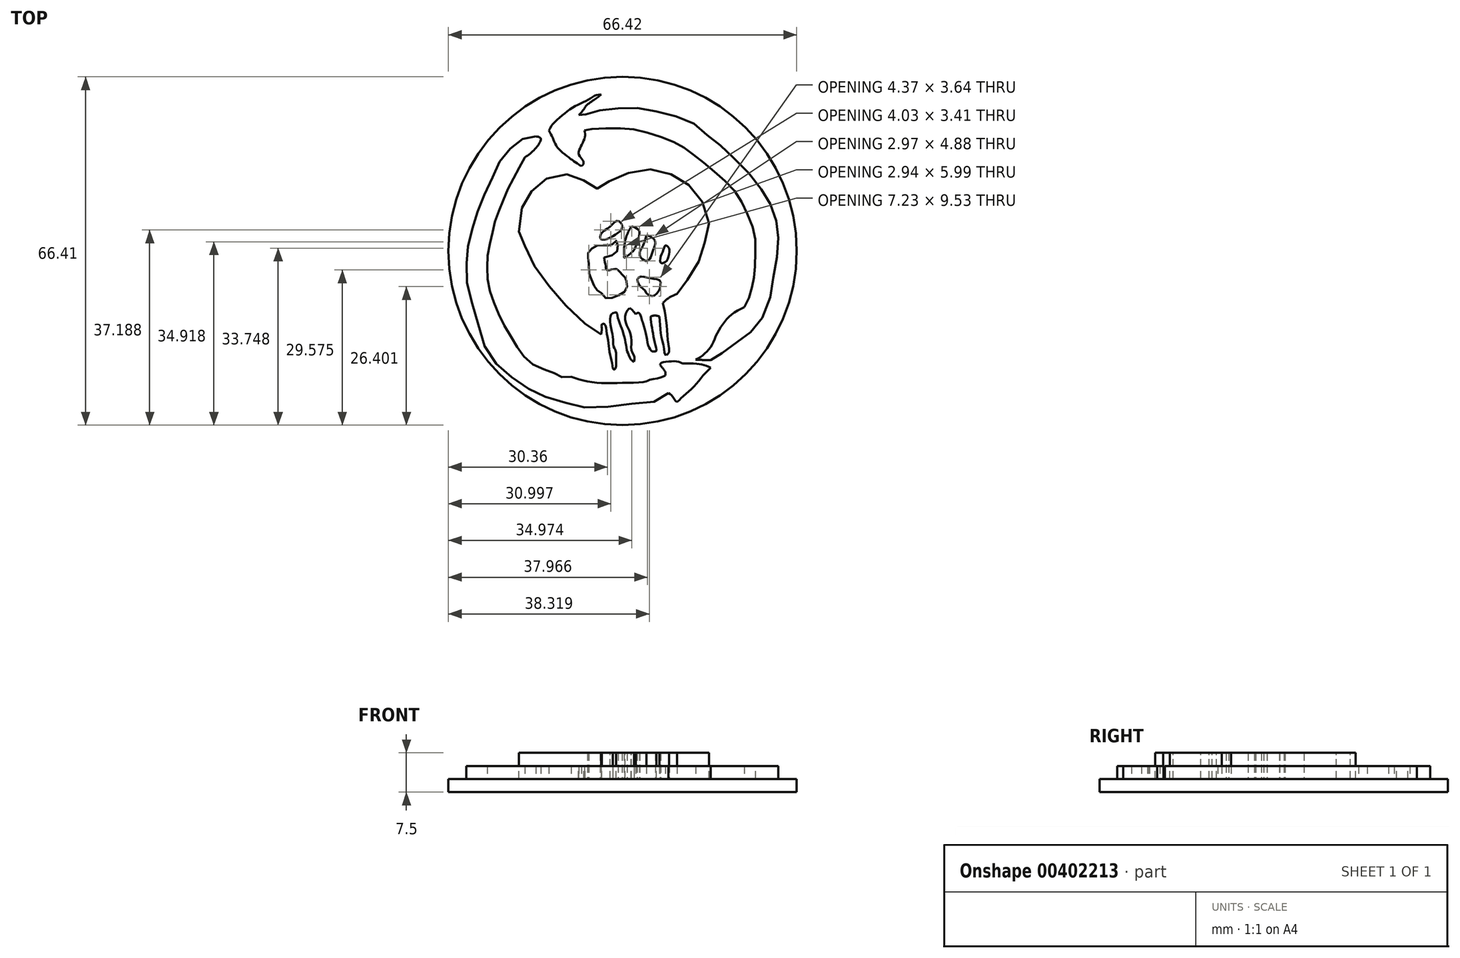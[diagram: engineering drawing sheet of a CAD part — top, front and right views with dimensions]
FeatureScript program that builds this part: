
annotation { "Feature Type Name" : "Feature", "Feature Type Description" : "" }
export const myFeature = defineFeature(function(context is Context, id is Id, definition is map)
    precondition{}
    {
        {
            var Q0;
            Q0=qCreatedBy(makeId("Top.planeOp"),FACE);
            var sketch = newSketch(context, id + "F0", { "sketchPlane" : qUnion([Q0])});
            skLineSegment(sketch, "E0", {"start": v(23.35, 42.94) * mm, "end": v(23.35, 78.4) * mm, "construction": true});
            skLineSegment(sketch, "E1", {"start": v(83.35, 42.94) * mm, "end": v(83.35, 78.4) * mm, "construction": true});
            skFitSpline(sketch, "E2", {"points": [v(67.3, 27.12) * mm, v(68.35, 27.69) * mm, v(69.45, 28.7) * mm, v(70.34, 29.8) * mm, v(70.99, 31.25) * mm, v(71.88, 33) * mm, v(73, 34.57) * mm, v(74.43, 35.94) * mm, v(76.6, 37.12) * mm], "startDerivative": vector(10.15, 4.67) * mm, "endDerivative": vector(15.46, 7.4) * mm});
            skFitSpline(sketch, "E3", {"points": [v(76.6, 37.12) * mm, v(77.58, 39.29) * mm, v(78.26, 41.84) * mm, v(78.56, 43.89) * mm, v(78.7, 48.13) * mm, v(78.44, 51.6) * mm, v(76.83, 55.52) * mm, v(75.11, 58.81) * mm, v(72.15, 61.84) * mm, v(68.8, 64.72) * mm, v(66, 66.88) * mm, v(63.48, 68.43) * mm, v(59.62, 69.94) * mm, v(55.35, 71.04) * mm, v(51.17, 71.25) * mm, v(47.04, 71.04) * mm, v(46.1, 70.83) * mm], "startDerivative": vector(19.98, 39.48) * mm, "endDerivative": vector(-22.77, -6.63) * mm});
            skFitSpline(sketch, "E4", {"points": [v(46.1, 70.83) * mm, v(46.23, 70.04) * mm, v(46.1, 69.31) * mm, v(45.66, 68.29) * mm, v(45.2, 67.32) * mm, v(44.97, 66.68) * mm, v(45.17, 65.94) * mm, v(45.63, 65.3) * mm, v(45.89, 64.83) * mm, v(45.89, 64.4) * mm, v(45.5, 64.03) * mm], "startDerivative": vector(1.88, -7.74) * mm, "endDerivative": vector(-5.78, -3.74) * mm});
            skFitSpline(sketch, "E5", {"points": [v(45.5, 64.03) * mm, v(44.46, 64.68) * mm, v(42.97, 65.75) * mm, v(40.94, 67.6) * mm, v(40.14, 69.15) * mm, v(39.32, 70.83) * mm], "startDerivative": vector(-6.2, 3.8) * mm, "endDerivative": vector(-4.35, 8.46) * mm});
            skFitSpline(sketch, "E6", {"points": [v(39.32, 70.83) * mm, v(40.06, 72.03) * mm, v(41.7, 73.56) * mm, v(43.58, 75.03) * mm, v(45.5, 76.06) * mm, v(46.98, 76.77) * mm, v(48.1, 77.5) * mm, v(49.24, 77.67) * mm], "startDerivative": vector(4.72, 9.25) * mm, "endDerivative": vector(9.94, 0.27) * mm});
            skFitSpline(sketch, "E7", {"points": [v(49.24, 77.67) * mm, v(48.43, 77) * mm, v(47.34, 76.29) * mm, v(46.35, 75.43) * mm, v(45.7, 74.52) * mm, v(45, 73.77) * mm], "startDerivative": vector(-3.85, -3.64) * mm, "endDerivative": vector(-3.85, -3.82) * mm});
            skFitSpline(sketch, "E8", {"points": [v(45, 73.77) * mm, v(45, 73.45) * mm, v(45.5, 73.58) * mm, v(47.34, 74.19) * mm, v(49.24, 74.71) * mm, v(52.43, 75.03) * mm, v(55.9, 75.11) * mm, v(59.24, 74.57) * mm, v(63.09, 73.62) * mm, v(66.58, 72.4) * mm, v(68.82, 70.55) * mm, v(70.71, 68.97) * mm, v(73.1, 67.07) * mm, v(75.28, 64.81) * mm, v(78.67, 61.33) * mm, v(80.4, 58.67) * mm, v(81.8, 56.27) * mm, v(82.74, 53.22) * mm, v(83.03, 50.62) * mm, v(82.85, 47.24) * mm, v(82.18, 43.21) * mm, v(81.65, 39.65) * mm, v(80.13, 35.33) * mm, v(78.05, 32.63) * mm, v(76.06, 31.08) * mm, v(73.43, 29.15) * mm, v(71.3, 27.7) * mm, v(70.18, 27.03) * mm], "startDerivative": vector(-5.92, -32.65) * mm, "endDerivative": vector(-40.98, -23.98) * mm});
            skFitSpline(sketch, "E9", {"points": [v(70.18, 27.03) * mm, v(69.09, 27.03) * mm, v(67.3, 27.12) * mm], "startDerivative": vector(-2.34, -0.03) * mm, "endDerivative": vector(-3.37, 0.2) * mm});
            skFitSpline(sketch, "E10", {"points": [v(36.82, 69.7) * mm, v(35.14, 69.55) * mm, v(33.17, 68.46) * mm, v(31.5, 66.83) * mm, v(29.77, 64.64) * mm, v(28.66, 62.13) * mm, v(27.1, 58.81) * mm, v(25.87, 55.87) * mm, v(24.97, 52.87) * mm, v(24.15, 50.12) * mm, v(23.69, 46.72) * mm, v(23.58, 44.48) * mm, v(23.94, 39.9) * mm, v(25.36, 35.88) * mm, v(26.4, 31.22) * mm, v(28.6, 27.12) * mm, v(31.3, 24.44) * mm, v(34.8, 22) * mm, v(37.4, 20.45) * mm, v(41.56, 19.18) * mm, v(45, 18.16) * mm, v(50.1, 18.1) * mm, v(55.46, 18.76) * mm, v(59.94, 19.22) * mm, v(62.1, 20.72) * mm], "startDerivative": vector(-57, 0.93) * mm, "endDerivative": vector(51.79, 49.17) * mm});
            skFitSpline(sketch, "E11", {"points": [v(62.1, 20.72) * mm, v(62.73, 20.28) * mm, v(63.44, 19.27) * mm, v(63.77, 19.11) * mm, v(64.78, 20.03) * mm, v(67, 22) * mm, v(68.9, 24.3) * mm, v(69.98, 25.36) * mm, v(70.18, 25.59) * mm], "startDerivative": vector(6.6, -3.28) * mm, "endDerivative": vector(2.54, 3.24) * mm});
            skFitSpline(sketch, "E12", {"points": [v(70.18, 25.59) * mm, v(68.84, 26.08) * mm, v(67.04, 26.36) * mm, v(64.95, 26.4) * mm, v(64.58, 26.49) * mm, v(63.8, 26.77) * mm, v(62.1, 26.75) * mm, v(60.72, 26.5) * mm, v(60.5, 26.1) * mm], "startDerivative": vector(-9.56, 3.9) * mm, "endDerivative": vector(-1.36, -5.85) * mm});
            skFitSpline(sketch, "E13", {"points": [v(60.5, 26.1) * mm, v(60.93, 25.59) * mm, v(61.5, 24.72) * mm, v(61.51, 24.12) * mm], "startDerivative": vector(1.24, -1.48) * mm, "endDerivative": vector(-0.27, -1.93) * mm});
            skFitSpline(sketch, "E14", {"points": [v(61.51, 24.12) * mm, v(60.54, 23.66) * mm, v(58.35, 23.24) * mm, v(57.8, 22.92) * mm, v(54.5, 22.71) * mm, v(49.9, 22.64) * mm, v(46.35, 23.01) * mm, v(43.58, 23.88) * mm], "startDerivative": vector(-8.1, -5.35) * mm, "endDerivative": vector(-17.12, 6.22) * mm});
            skFitSpline(sketch, "E15", {"points": [v(43.58, 23.88) * mm, v(41.49, 23.88) * mm, v(39.92, 24.74) * mm, v(36.88, 25.85) * mm, v(34.29, 28.06) * mm, v(32.52, 30.77) * mm, v(30.51, 34.2) * mm, v(29.01, 37.53) * mm, v(27.88, 40.85) * mm, v(27.55, 44.26) * mm, v(27.7, 47.57) * mm, v(28.47, 50.94) * mm, v(29.1, 53.73) * mm, v(30.23, 56.55) * mm, v(31.54, 59.7) * mm, v(33.14, 62.78) * mm, v(34.71, 65.67) * mm], "startDerivative": vector(-44.4, -5.35) * mm, "endDerivative": vector(24.37, 45.13) * mm});
            skFitSpline(sketch, "E16", {"points": [v(34.71, 65.67) * mm, v(36.23, 66.86) * mm, v(37.41, 68.25) * mm, v(37.76, 69.12) * mm, v(37.55, 69.47) * mm, v(36.82, 69.7) * mm], "startDerivative": vector(5.88, 4.17) * mm, "endDerivative": vector(-4.96, 1.04) * mm});
            skFitSpline(sketch, "E17", {"points": [v(49.24, 31.89) * mm, v(46.77, 33.5) * mm, v(42.83, 37.12) * mm, v(39.32, 41.14) * mm, v(36.4, 45.23) * mm, v(34.71, 48.82) * mm, v(33.8, 49.97) * mm, v(33.8, 54.46) * mm, v(34.71, 57.4) * mm, v(36.82, 60.1) * mm, v(39.32, 61.85) * mm, v(42.88, 62.45) * mm, v(45, 61.85) * mm, v(47.87, 59.9) * mm, v(48.52, 59.75) * mm, v(49.24, 60.2) * mm, v(51.66, 61.55) * mm, v(55.16, 62.9) * mm, v(59.15, 63.4) * mm, v(62.7, 62.4) * mm, v(65.74, 60.65) * mm, v(68.18, 57.86) * mm, v(69.78, 53.81) * mm, v(69.42, 50.7) * mm, v(68.3, 47.32) * mm, v(67.3, 44.53) * mm, v(64.91, 41.33) * mm, v(63.73, 39.67) * mm], "startDerivative": vector(-63.83, 44.64) * mm, "endDerivative": vector(-34.2, -51.43) * mm});
            skFitSpline(sketch, "E18", {"points": [v(63.73, 39.67) * mm, v(62.1, 38.84) * mm, v(61.03, 37.92) * mm], "startDerivative": vector(-3.27, -1.45) * mm, "endDerivative": vector(-2.1, -2.05) * mm});
            skFitSpline(sketch, "E19", {"points": [v(61.03, 37.92) * mm, v(61.51, 35.7) * mm, v(61.83, 32.7) * mm, v(62.1, 30.03) * mm, v(62.1, 28.26) * mm, v(61.51, 28.03) * mm, v(61.25, 29.15) * mm, v(60.84, 31.1) * mm, v(60.54, 33.1) * mm, v(60.35, 35.36) * mm], "startDerivative": vector(4.31, -17.45) * mm, "endDerivative": vector(-1.52, 18.9) * mm});
            skFitSpline(sketch, "E20", {"points": [v(60.35, 35.36) * mm, v(59.52, 35.53) * mm, v(58.7, 35.36) * mm], "startDerivative": vector(-1.66, 0.49) * mm, "endDerivative": vector(-1.64, -0.5) * mm});
            skFitSpline(sketch, "E21", {"points": [v(58.7, 35.36) * mm, v(58.88, 33.76) * mm, v(59.14, 32.07) * mm, v(59.53, 30.35) * mm, v(59.77, 29.15) * mm, v(59.72, 28.72) * mm, v(59.43, 28.64) * mm, v(58.98, 28.72) * mm, v(58.7, 29.03) * mm, v(58.2, 29.81) * mm, v(57.92, 31.56) * mm], "startDerivative": vector(1.28, -12.38) * mm, "endDerivative": vector(-4.36, 14.52) * mm});
            skFitSpline(sketch, "E22", {"points": [v(57.92, 31.56) * mm, v(57.6, 32.88) * mm, v(57.35, 33.77) * mm, v(57, 34.78) * mm, v(56.58, 35.91) * mm, v(56.18, 36.03) * mm, v(55.87, 35.78) * mm], "startDerivative": vector(-1.53, 7.65) * mm, "endDerivative": vector(-2.56, -2.52) * mm});
            skFitSpline(sketch, "E23", {"points": [v(55.87, 35.78) * mm, v(55.17, 36.58) * mm, v(54.75, 36.9) * mm, v(54.2, 36.43) * mm, v(53.85, 35.36) * mm, v(54, 34.1) * mm, v(54.49, 33.02) * mm, v(54.89, 31.79) * mm, v(55.04, 30.24) * mm, v(55.04, 28.95) * mm, v(55.43, 28.07) * mm, v(55.62, 27.42) * mm, v(55.55, 26.71) * mm], "startDerivative": vector(-8.64, 9.85) * mm, "endDerivative": vector(-1.83, -10.3) * mm});
            skFitSpline(sketch, "E24", {"points": [v(55.55, 26.71) * mm, v(54.93, 27.12) * mm, v(54.5, 28.16) * mm, v(54.2, 28.74) * mm, v(54.03, 29.7) * mm, v(53.79, 31.02) * mm, v(53.33, 32.68) * mm, v(52.8, 34.07) * mm, v(52.36, 35.52) * mm, v(52.27, 36.03) * mm, v(51.92, 36.13) * mm], "startDerivative": vector(-7.89, 3.3) * mm, "endDerivative": vector(-7, 0.68) * mm});
            skFitSpline(sketch, "E25", {"points": [v(51.92, 36.13) * mm, v(51.28, 35.83) * mm, v(51.03, 35.36) * mm, v(50.98, 34.56) * mm, v(51.14, 33.2) * mm, v(51.39, 32) * mm, v(51.55, 31.02) * mm, v(51.6, 29.62) * mm, v(51.92, 29.16) * mm, v(52.15, 28.04) * mm, v(52.13, 26.57) * mm, v(52.08, 25.59) * mm, v(51.72, 25.23) * mm, v(51.48, 25.44) * mm], "startDerivative": vector(-10.52, -3.53) * mm, "endDerivative": vector(-4.82, 6.8) * mm});
            skFitSpline(sketch, "E26", {"points": [v(51.48, 25.44) * mm, v(51.32, 26.55) * mm, v(51.02, 27.82) * mm, v(50.82, 29.13) * mm, v(50.65, 30.45) * mm, v(50.36, 32) * mm, v(50.17, 33.33) * mm, v(49.85, 33.91) * mm, v(49.53, 33.91) * mm, v(49.36, 33.77) * mm, v(49.36, 33.36) * mm, v(49.4, 32.76) * mm, v(49.24, 31.89) * mm], "startDerivative": vector(-1.3, 11.61) * mm, "endDerivative": vector(-2.77, -12.26) * mm});
            skFitSpline(sketch, "E27", {"points": [v(58.96, 39.22) * mm, v(59.6, 39.48) * mm, v(60.35, 40.38) * mm, v(60.54, 41.23) * mm, v(60.63, 41.93) * mm, v(60.16, 42.4) * mm, v(59.15, 42.56) * mm, v(58.05, 42.79) * mm, v(57.03, 42.95) * mm, v(56.37, 42.74) * mm, v(56.15, 42.31) * mm, v(56.4, 41.57) * mm, v(56.94, 40.89) * mm, v(57.58, 40.37) * mm, v(57.92, 39.75) * mm, v(58.96, 39.22) * mm]});
            skFitSpline(sketch, "E28", {"points": [v(54.11, 41.93) * mm, v(54.2, 41.05) * mm, v(53.57, 39.92) * mm, v(51.85, 39.08) * mm, v(50.25, 38.83) * mm, v(49.12, 40) * mm, v(48.28, 40.5) * mm, v(47.65, 41.93) * mm, v(46.98, 43.49) * mm, v(46.85, 46.38) * mm, v(46.69, 47.18) * mm, v(47.27, 48.06) * mm, v(48.45, 48.86) * mm, v(49.92, 48.94) * mm, v(50.97, 48.98) * mm, v(51.51, 49.2) * mm, v(52.18, 49.78) * mm, v(52.48, 48.6) * mm, v(52.02, 47.43) * mm, v(49.83, 46.55) * mm], "startDerivative": vector(4.55, -19.88) * mm, "endDerivative": vector(-37.25, -10.48) * mm});
            skFitSpline(sketch, "E29", {"points": [v(49.83, 46.55) * mm, v(50.17, 44.66) * mm, v(50.42, 44.16) * mm, v(51.93, 44.4) * mm, v(52.81, 43.82) * mm, v(53.86, 42.65) * mm, v(54.11, 41.93) * mm], "startDerivative": vector(1.83, -9.93) * mm, "endDerivative": vector(1.03, -5.14) * mm});
            skFitSpline(sketch, "E30", {"points": [v(49.12, 50.16) * mm, v(50.25, 50.07) * mm, v(51.93, 50.91) * mm, v(53.1, 51.88) * mm, v(53.2, 52.93) * mm, v(52.35, 53.6) * mm, v(50.92, 52.47) * mm, v(49.37, 51.25) * mm, v(49.12, 50.16) * mm]});
            skFitSpline(sketch, "E31", {"points": [v(53.7, 47.01) * mm, v(53.65, 48.4) * mm, v(54.11, 50.75) * mm, v(55.08, 52.55) * mm], "startDerivative": vector(-0.38, 4.5) * mm, "endDerivative": vector(3.1, 4.86) * mm});
            skFitSpline(sketch, "E32", {"points": [v(55.08, 52.55) * mm, v(56.47, 51.75) * mm, v(56.38, 50.24) * mm, v(55.63, 48.19) * mm, v(54.95, 47.43) * mm, v(53.7, 46.55) * mm, v(53.7, 47.01) * mm], "startDerivative": vector(9.19, -3.02) * mm, "endDerivative": vector(1.49, 6.56) * mm});
            skFitSpline(sketch, "E33", {"points": [v(56.8, 46.55) * mm, v(56.63, 47.56) * mm, v(57.22, 48.82) * mm, v(57.9, 50.83) * mm], "startDerivative": vector(-1.2, 3.63) * mm, "endDerivative": vector(1.45, 5.36) * mm});
            skFitSpline(sketch, "E34", {"points": [v(57.9, 50.83) * mm, v(58.82, 50.5) * mm, v(59.49, 49.86) * mm, v(59.57, 49.07) * mm, v(59.2, 48.02) * mm, v(58.65, 46.55) * mm, v(57.9, 45.92) * mm, v(56.8, 46.55) * mm], "startDerivative": vector(6.96, -1.96) * mm, "endDerivative": vector(-7.33, 6.23) * mm});
            skFitSpline(sketch, "E35", {"points": [v(60.5, 46) * mm, v(60.87, 47.39) * mm, v(61.3, 48.52) * mm, v(61.54, 48.9) * mm, v(62.17, 48.48) * mm, v(62.26, 47.68) * mm, v(61.88, 46.13) * mm, v(61.33, 45.63) * mm, v(60.75, 45.5) * mm, v(60.5, 46) * mm]});
            skSolve(sketch);
        }
        {
            var Q0;
            Q0=makeQuery(id+"F0.imprint","IMPRINT",FACE,{"disambiguationData":[TD([[makeQuery(id+"F0.imprint","IMPRINT",EDGE,{"derivedFrom":sQuery(id+"F0.wireOp",EDGE,"E10")}),1.0]])]});
            var Q1;
            Q1=makeQuery(id+"F0.imprint","IMPRINT",FACE,{"disambiguationData":[TD([[makeQuery(id+"F0.imprint","IMPRINT",EDGE,{"derivedFrom":sQuery(id+"F0.wireOp",EDGE,"E2")}),-1.0]])]});
            extrude(context, id + "F1", {"entities" : qUnion([Q0, Q1]), "depth" : 2.5 * mm});
        }
        {
            var Q0;
            Q0=makeQuery(id+"F0.imprint","IMPRINT",FACE,{"disambiguationData":[TD([[makeQuery(id+"F0.imprint","IMPRINT",EDGE,{"derivedFrom":sQuery(id+"F0.wireOp",EDGE,"E17")}),-1.0]])]});
            extrude(context, id + "F2", {"entities" : qUnion([Q0]), "depth" : 5 * mm});
        }
        {
            var Q0;
            Q0=makeQuery(id+"F2.opExtrude","CAP_FACE",FACE,{"disambiguationData":[OSD([sQuery(id+"F0.wireOp",EDGE,"E17"),sQuery(id+"F0.wireOp",EDGE,"E18"),sQuery(id+"F0.wireOp",EDGE,"E19"),sQuery(id+"F0.wireOp",EDGE,"E20"),sQuery(id+"F0.wireOp",EDGE,"E21"),sQuery(id+"F0.wireOp",EDGE,"E22"),sQuery(id+"F0.wireOp",EDGE,"E23"),sQuery(id+"F0.wireOp",EDGE,"E24"),sQuery(id+"F0.wireOp",EDGE,"E25"),sQuery(id+"F0.wireOp",EDGE,"E26"),sQuery(id+"F0.wireOp",EDGE,"E27"),sQuery(id+"F0.wireOp",EDGE,"E28"),sQuery(id+"F0.wireOp",EDGE,"E29"),sQuery(id+"F0.wireOp",EDGE,"E30"),sQuery(id+"F0.wireOp",EDGE,"E31"),sQuery(id+"F0.wireOp",EDGE,"E32"),sQuery(id+"F0.wireOp",EDGE,"E33"),sQuery(id+"F0.wireOp",EDGE,"E34"),sQuery(id+"F0.wireOp",EDGE,"E35")])],"isStart":true});
            var sketch = newSketch(context, id + "F3", { "sketchPlane" : qUnion([Q0])});
            skLineSegment(sketch, "E36", {"start": v(23.35, -42.94) * mm, "end": v(83.35, -42.94) * mm, "construction": true});
            skLineSegment(sketch, "E37", {"start": v(53.35, -42.94) * mm, "end": v(53.35, -78.81) * mm, "construction": true});
            skCircle(sketch, "E38", {"center": v(53.35, -47.84) * mm, "radius": 33.2 * mm});
            skSolve(sketch);
        }
        {
            var Q0;
            Q0 = qSketchRegion(id + "F3", true);
            extrude(context, id + "F4", {"entities" : qUnion([Q0]), "depth" : 2.5 * mm});
        }
    });
